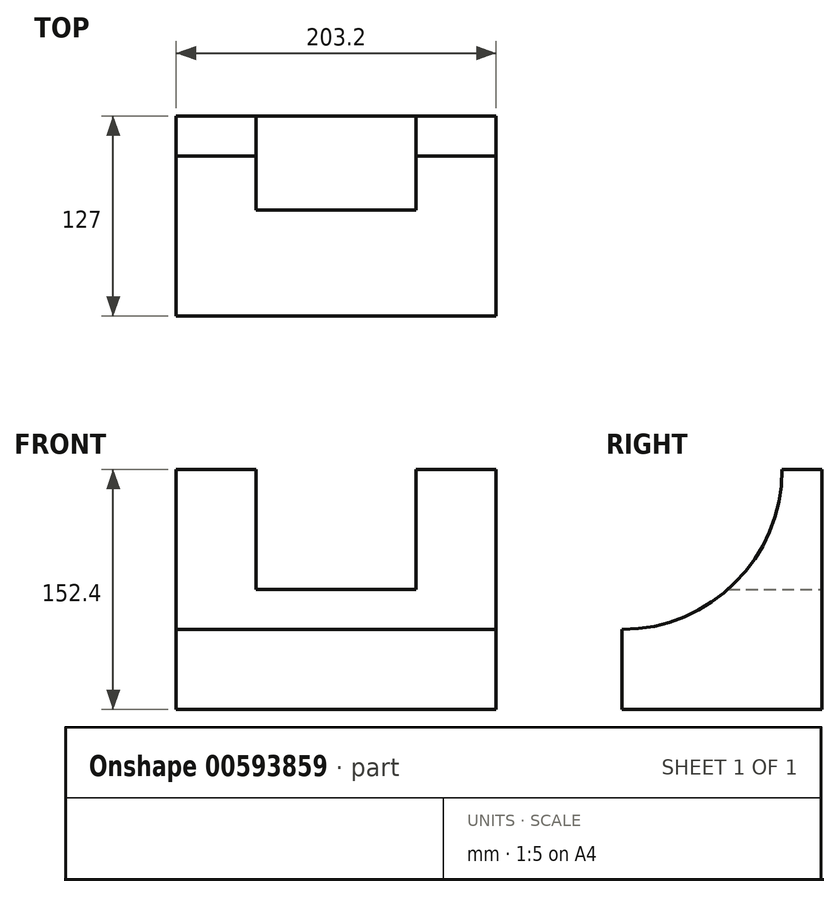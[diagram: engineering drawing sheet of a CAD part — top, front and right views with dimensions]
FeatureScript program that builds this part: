
annotation { "Feature Type Name" : "Feature", "Feature Type Description" : "" }
export const myFeature = defineFeature(function(context is Context, id is Id, definition is map)
    precondition{}
    {
        {
            var Q0;
            Q0=qCreatedBy(makeId("Front.planeOp"),FACE);
            var sketch = newSketch(context, id + "F0", { "sketchPlane" : qUnion([Q0])});
            skLineSegment(sketch, "E0.bottom", {"start": v(101.6, 76.2) * mm, "end": v(50.8, 76.2) * mm});
            skLineSegment(sketch, "E0.top", {"start": v(101.6, -76.2) * mm, "end": v(-101.6, -76.2) * mm});
            skLineSegment(sketch, "E0.left", {"start": v(101.6, 76.2) * mm, "end": v(101.6, -76.2) * mm});
            skLineSegment(sketch, "E0.right", {"start": v(-101.6, 76.2) * mm, "end": v(-101.6, -76.2) * mm});
            skPoint(sketch, "E0.middle", {"position": v(0, 0) * mm});
            skLineSegment(sketch, "E1", {"start": v(-50.8, 76.2) * mm, "end": v(-50.8, 0) * mm});
            skLineSegment(sketch, "E2", {"start": v(-50.8, 0) * mm, "end": v(50.8, 0) * mm});
            skLineSegment(sketch, "E3", {"start": v(50.8, 0) * mm, "end": v(50.8, 76.2) * mm});
            skLineSegment(sketch, "E4.trimOffspring", {"start": v(-50.8, 76.2) * mm, "end": v(-101.6, 76.2) * mm});
            skSolve(sketch);
        }
        {
            var Q0;
            Q0=makeQuery(id+"F0.imprint","IMPRINT",FACE,{"disambiguationData":[TD([[makeQuery(id+"F0.imprint","IMPRINT",EDGE,{"derivedFrom":sQuery(id+"F0.wireOp",EDGE,"E0.bottom")}),1.0]])]});
            extrude(context, id + "F1", {"entities" : qUnion([Q0]), "depth" : 127 * mm, "offsetDistance" : 25.4 * mm});
        }
        {
            var Q0;
            Q0=makeQuery(id+"F1.opExtrude","SWEPT_FACE",FACE,{"disambiguationData":[OSD([sQuery(id+"F0.wireOp",EDGE,"E0.left")])]});
            var sketch = newSketch(context, id + "F2", { "sketchPlane" : qUnion([Q0])});
            skCircle(sketch, "E5", {"center": v(-127, 76.2) * mm, "radius": 101.6 * mm});
            skSolve(sketch);
        }
        {
            var Q0;
            {var subQ0=sQuery(id+"F2.wireOp",EDGE,"E5");var subQ1=sQuery(id+"F0.wireOp",EDGE,"E0.left");var subQ4=makeQuery(id+"F1.opExtrude","CAP_EDGE",EDGE,{"disambiguationData":[OSD([subQ1])],"isStart":false});var subQ5=makeQuery(id+"F2.imprint","INTERSECT",VERTEX,{"derivedFrom":[subQ4,subQ0]});Q0=makeQuery(id+"F2.imprint","IMPRINT",FACE,{"disambiguationData":[TD([[makeQuery(id+"F2.imprint","IMPRINT",EDGE,{"disambiguationData":[TD([[subQ5,-1.0]])],"derivedFrom":subQ0}),1.0]])]});}
            extrude(context, id + "F3", {"entities" : qUnion([Q0]), "operationType" : NewBodyOperationType.REMOVE, "endBound" : BoundingType.THROUGH_ALL, "oppositeDirection" : true, "depth" : 25.4 * mm, "offsetDistance" : 25.4 * mm});
        }
    });
